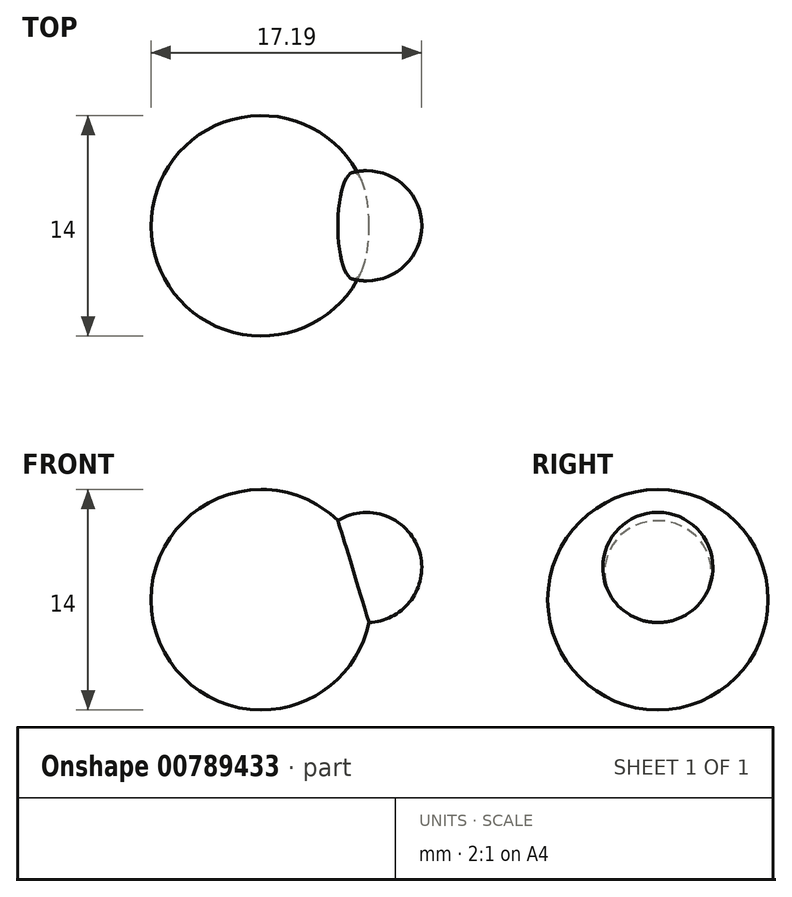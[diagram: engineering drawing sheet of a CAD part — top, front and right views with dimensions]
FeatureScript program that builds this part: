
annotation { "Feature Type Name" : "Feature", "Feature Type Description" : "" }
export const myFeature = defineFeature(function(context is Context, id is Id, definition is map)
    precondition{}
    {
        {
            var Q0;
            Q0=qCreatedBy(makeId("Front.planeOp"),FACE);
            var sketch = newSketch(context, id + "F0", { "sketchPlane" : qUnion([Q0])});
            skLineSegment(sketch, "E0", {"start": v(0, 0) * mm, "end": v(0, 14) * mm});
            skArc(sketch, "E1", {"start": v(0, 0) * mm, "mid": v(7, 7) * mm, "end": v(0, 14) * mm});
            skSolve(sketch);
        }
        {
            var Q0;
            Q0=qCreatedBy(makeId("Front.planeOp"),FACE);
            var sketch = newSketch(context, id + "F1", { "sketchPlane" : qUnion([Q0])});
            skLineSegment(sketch, "E2", {"start": v(0, 0) * mm, "end": v(0, 14) * mm, "construction": true});
            skLineSegment(sketch, "E3", {"start": v(0, 7) * mm, "end": v(6.7, 9.05) * mm, "construction": true});
            skSolve(sketch);
        }
        {
            var Q0;
            Q0=sQuery(id+"F1.wireOp",VERTEX,"E3.end");
            var Q1;
            Q1=sQuery(id+"F1.wireOp",EDGE,"E3");
            cPlane(context, id + "F2", {"entities" : qUnion([Q0, Q1]), "cplaneType" : CPlaneType.LINE_POINT, "offset" : 25 * mm, "width" : 150 * mm, "height" : 150 * mm});
        }
        {
            var Q0;
            Q0 = qSketchRegion(id + "F0", true);
            var Q1;
            Q1=sQuery(id+"F1.wireOp",EDGE,"E2");
            revolve(context, id + "F3", {"surfaceOperationType" : NewSurfaceOperationType.NEW, "entities" : qUnion([Q0]), "axis" : qUnion([Q1]), "revolveType" : RevolveType.FULL});
        }
        {
            var Q0;
            Q0=qCreatedBy(id+"F2.planeOp",FACE);
            var sketch = newSketch(context, id + "F4", { "sketchPlane" : qUnion([Q0])});
            skLineSegment(sketch, "E4", {"start": v(-3.5, 6.7) * mm, "end": v(3.5, 6.7) * mm});
            skArc(sketch, "E5", {"start": v(-3.5, 6.7) * mm, "mid": v(0, 3.2) * mm, "end": v(3.5, 6.7) * mm});
            skSolve(sketch);
        }
        {
            var Q0;
            Q0=makeQuery(id+"F4.imprint","IMPRINT",FACE,{"disambiguationData":[TD([[makeQuery(id+"F4.imprint","IMPRINT",EDGE,{"derivedFrom":sQuery(id+"F4.wireOp",EDGE,"E4")}),-1.0]])]});
            var Q1;
            Q1=sQuery(id+"F4.wireOp",EDGE,"E4");
            revolve(context, id + "F5", {"operationType" : NewBodyOperationType.ADD, "surfaceOperationType" : NewSurfaceOperationType.NEW, "entities" : qUnion([Q0]), "axis" : qUnion([Q1]), "revolveType" : RevolveType.FULL});
        }
    });
